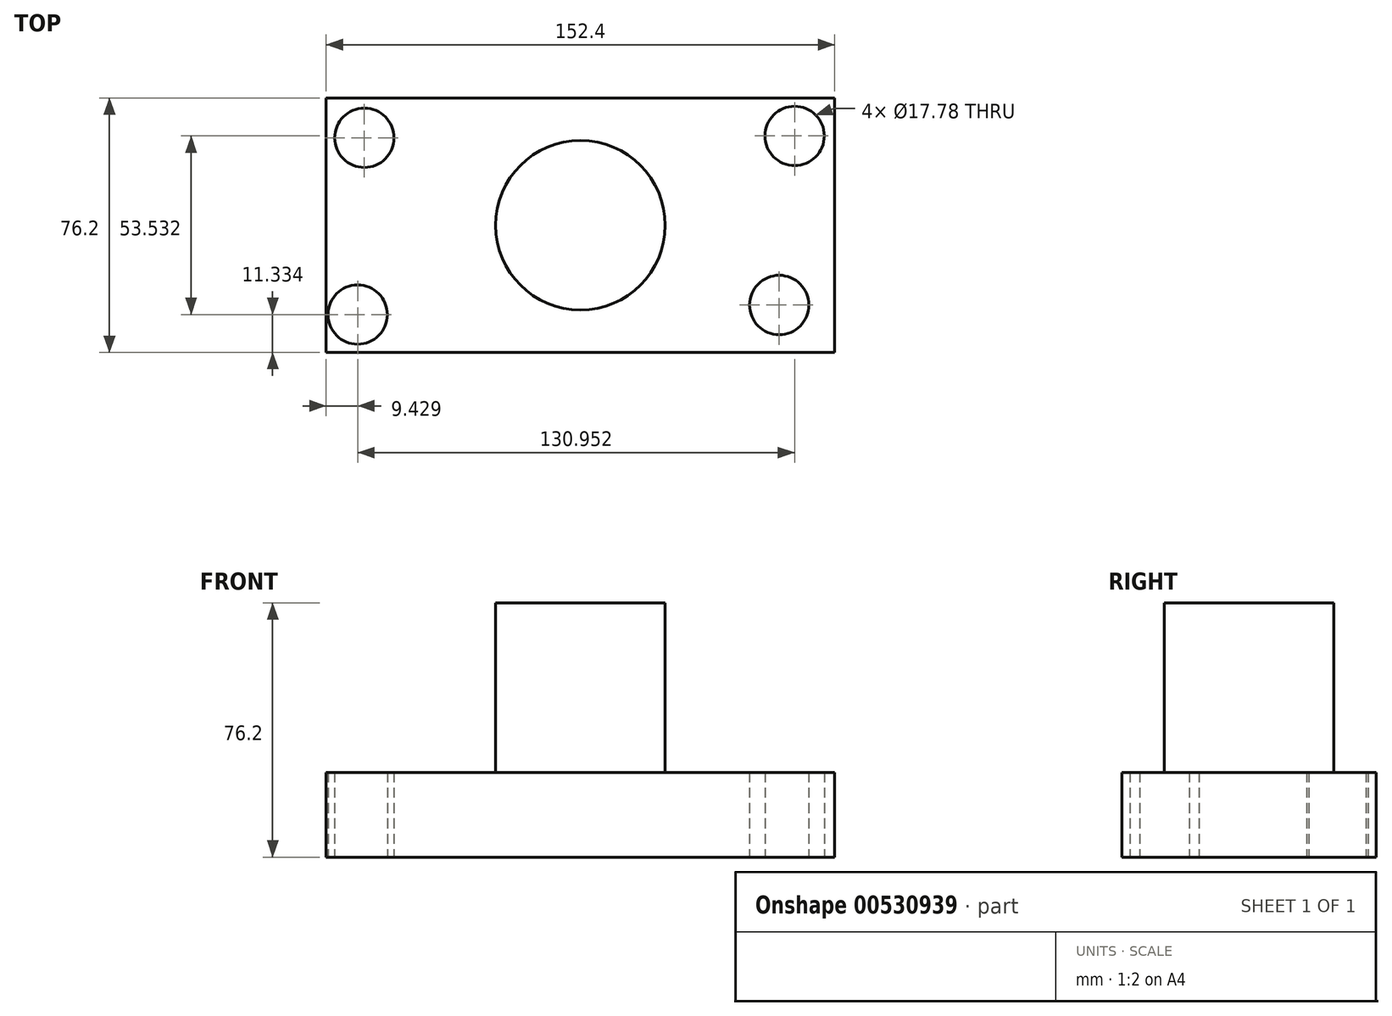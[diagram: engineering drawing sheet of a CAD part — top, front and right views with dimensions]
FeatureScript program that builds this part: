
annotation { "Feature Type Name" : "Feature", "Feature Type Description" : "" }
export const myFeature = defineFeature(function(context is Context, id is Id, definition is map)
    precondition{}
    {
        {
            var Q0;
            Q0=qCreatedBy(makeId("Top.planeOp"),FACE);
            var sketch = newSketch(context, id + "F0", { "sketchPlane" : qUnion([Q0])});
            skLineSegment(sketch, "E0.bottom", {"start": v(76.2, 38.1) * mm, "end": v(-76.2, 38.1) * mm});
            skLineSegment(sketch, "E0.top", {"start": v(76.2, -38.1) * mm, "end": v(-76.2, -38.1) * mm});
            skLineSegment(sketch, "E0.left", {"start": v(76.2, 38.1) * mm, "end": v(76.2, -38.1) * mm});
            skLineSegment(sketch, "E0.right", {"start": v(-76.2, 38.1) * mm, "end": v(-76.2, -38.1) * mm});
            skPoint(sketch, "E0.middle", {"position": v(0, 0) * mm});
            skCircle(sketch, "E1", {"center": v(-64.76, 26.2) * mm, "radius": 8.9 * mm});
            skCircle(sketch, "E2", {"center": v(-66.77, -26.77) * mm, "radius": 8.9 * mm});
            skCircle(sketch, "E3", {"center": v(64.18, 26.77) * mm, "radius": 8.9 * mm});
            skCircle(sketch, "E4", {"center": v(59.58, -23.89) * mm, "radius": 8.9 * mm});
            skSolve(sketch);
        }
        {
            var Q0;
            Q0=makeQuery(id+"F0.imprint","IMPRINT",FACE,{"disambiguationData":[TD([[makeQuery(id+"F0.imprint","IMPRINT",EDGE,{"derivedFrom":sQuery(id+"F0.wireOp",EDGE,"E0.bottom")}),1.0]])]});
            extrude(context, id + "F1", {"entities" : qUnion([Q0]), "depth" : 25.4 * mm, "offsetDistance" : 25.4 * mm});
        }
        {
            var Q0;
            Q0=qCreatedBy(makeId("Front.planeOp"),FACE);
            var sketch = newSketch(context, id + "F2", { "sketchPlane" : qUnion([Q0])});
            skLineSegment(sketch, "E5.bottom", {"start": v(0, 25.4) * mm, "end": v(25.4, 25.4) * mm});
            skLineSegment(sketch, "E5.top", {"start": v(0, 76.2) * mm, "end": v(25.4, 76.2) * mm});
            skLineSegment(sketch, "E5.left", {"start": v(0, 25.4) * mm, "end": v(0, 76.2) * mm});
            skLineSegment(sketch, "E5.right", {"start": v(25.4, 25.4) * mm, "end": v(25.4, 76.2) * mm});
            skSolve(sketch);
        }
        {
            var Q0;
            Q0=makeQuery(id+"F2.imprint","IMPRINT",FACE,{"disambiguationData":[TD([[makeQuery(id+"F2.imprint","IMPRINT",EDGE,{"derivedFrom":sQuery(id+"F2.wireOp",EDGE,"E5.bottom")}),1.0]])]});
            var Q1;
            Q1=sQuery(id+"F2.wireOp",EDGE,"E5.left");
            revolve(context, id + "F3", {"operationType" : NewBodyOperationType.ADD, "entities" : qUnion([Q0]), "axis" : qUnion([Q1]), "revolveType" : RevolveType.FULL});
        }
    });
